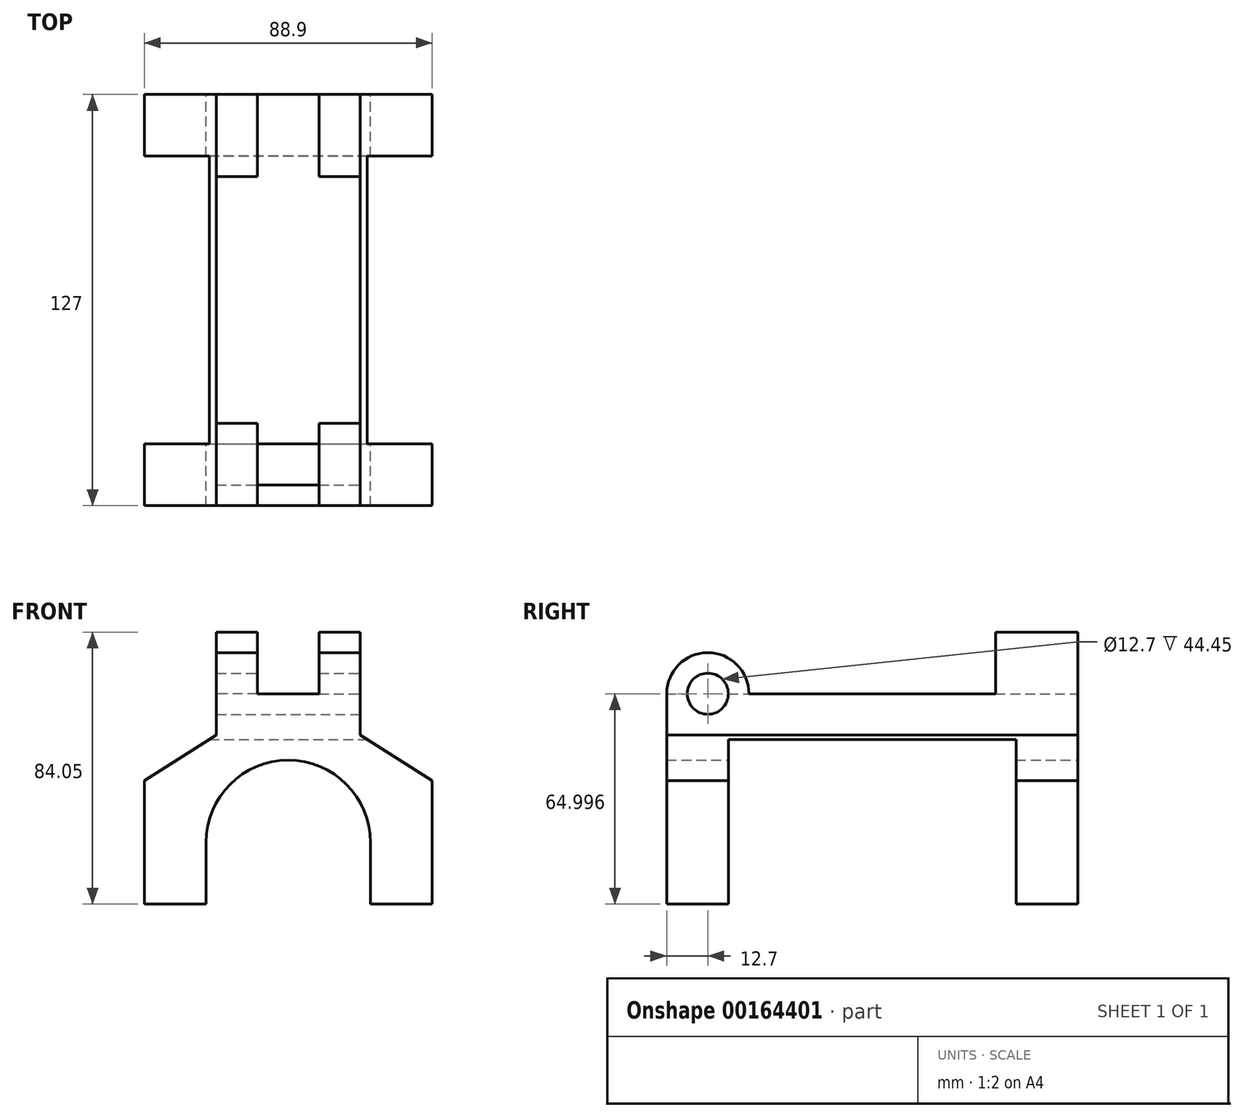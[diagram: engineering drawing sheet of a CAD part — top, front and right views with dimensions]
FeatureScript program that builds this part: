
annotation { "Feature Type Name" : "Feature", "Feature Type Description" : "" }
export const myFeature = defineFeature(function(context is Context, id is Id, definition is map)
    precondition{}
    {
        {
            var Q0;
            Q0=qCreatedBy(makeId("Front.planeOp"),FACE);
            var sketch = newSketch(context, id + "F0", { "sketchPlane" : qUnion([Q0])});
            skLineSegment(sketch, "E0.bottom", {"start": v(44.45, 0) * mm, "end": v(25.4, 0) * mm});
            skLineSegment(sketch, "E0.top", {"start": v(44.45, -19.05) * mm, "end": v(25.4, -19.05) * mm});
            skLineSegment(sketch, "E0.left", {"start": v(44.45, 0) * mm, "end": v(44.45, -19.05) * mm});
            skLineSegment(sketch, "E0.right", {"start": v(25.4, 0) * mm, "end": v(25.4, -19.05) * mm});
            skPoint(sketch, "E0.middle", {"position": v(34.92, -9.53) * mm});
            skLineSegment(sketch, "E1.bottom", {"start": v(-25.4, 0) * mm, "end": v(-44.45, 0) * mm});
            skLineSegment(sketch, "E1.top", {"start": v(-25.4, -19.05) * mm, "end": v(-44.45, -19.05) * mm});
            skLineSegment(sketch, "E1.left", {"start": v(-25.4, 0) * mm, "end": v(-25.4, -19.05) * mm});
            skLineSegment(sketch, "E1.right", {"start": v(-44.45, 0) * mm, "end": v(-44.45, -19.05) * mm});
            skPoint(sketch, "E1.middle", {"position": v(-34.93, -9.52) * mm});
            skPoint(sketch, "E1.middle.positionSnap0", {"position": v(25.4, -9.53) * mm});
            skPoint(sketch, "E1.centerSnap0", {"position": v(25.4, -9.53) * mm});
            skArc(sketch, "E2", {"start": v(25.4, 0) * mm, "mid": v(0, 25.4) * mm, "end": v(-25.4, 0) * mm});
            skLineSegment(sketch, "E3", {"start": v(44.45, 0) * mm, "end": v(44.45, 19.05) * mm});
            skLineSegment(sketch, "E4", {"start": v(-44.45, 0) * mm, "end": v(-44.45, 19.05) * mm});
            skLineSegment(sketch, "E5", {"start": v(-44.45, 19.05) * mm, "end": v(-22.23, 33.25) * mm});
            skLineSegment(sketch, "E6", {"start": v(-44.45, 19.05) * mm, "end": v(-22.23, 19.05) * mm});
            skLineSegment(sketch, "E7", {"start": v(-22.23, 19.05) * mm, "end": v(-22.23, 33.25) * mm});
            skLineSegment(sketch, "E8", {"start": v(44.45, 19.05) * mm, "end": v(22.22, 19.05) * mm});
            skLineSegment(sketch, "E9", {"start": v(22.22, 19.05) * mm, "end": v(22.22, 33.25) * mm});
            skLineSegment(sketch, "E10", {"start": v(22.22, 33.25) * mm, "end": v(44.45, 19.05) * mm});
            skLineSegment(sketch, "E11", {"start": v(22.22, 33.25) * mm, "end": v(-22.23, 33.25) * mm});
            skSolve(sketch);
        }
        {
            var Q0;
            Q0=makeQuery(id+"F0.imprint","IMPRINT",FACE,{"disambiguationData":[TD([[makeQuery(id+"F0.imprint","IMPRINT",EDGE,{"derivedFrom":sQuery(id+"F0.wireOp",EDGE,"E0.bottom")}),-1.0]])]});
            var Q1;
            Q1=makeQuery(id+"F0.imprint","IMPRINT",FACE,{"disambiguationData":[TD([[makeQuery(id+"F0.imprint","IMPRINT",EDGE,{"derivedFrom":sQuery(id+"F0.wireOp",EDGE,"E8")}),-1.0]])]});
            var Q2;
            Q2=makeQuery(id+"F0.imprint","IMPRINT",FACE,{"disambiguationData":[TD([[makeQuery(id+"F0.imprint","IMPRINT",EDGE,{"derivedFrom":sQuery(id+"F0.wireOp",EDGE,"E0.bottom")}),1.0]])]});
            var Q3;
            Q3=makeQuery(id+"F0.imprint","IMPRINT",FACE,{"disambiguationData":[TD([[makeQuery(id+"F0.imprint","IMPRINT",EDGE,{"derivedFrom":sQuery(id+"F0.wireOp",EDGE,"E1.bottom")}),1.0]])]});
            var Q4;
            Q4=makeQuery(id+"F0.imprint","IMPRINT",FACE,{"disambiguationData":[TD([[makeQuery(id+"F0.imprint","IMPRINT",EDGE,{"derivedFrom":sQuery(id+"F0.wireOp",EDGE,"E5")}),-1.0]])]});
            extrude(context, id + "F1", {"entities" : qUnion([Q0, Q1, Q2, Q3, Q4]), "depth" : 127 * mm});
        }
        {
            var Q0;
            Q0=makeQuery(id+"F1.opExtrude","SWEPT_FACE",FACE,{"disambiguationData":[OSD([sQuery(id+"F0.wireOp",EDGE,"E0.left"),sQuery(id+"F0.wireOp",EDGE,"E3")])]});
            var sketch = newSketch(context, id + "F2", { "sketchPlane" : qUnion([Q0])});
            skLineSegment(sketch, "E12", {"start": v(-127, 19.05) * mm, "end": v(-127, -19.05) * mm});
            skLineSegment(sketch, "E13", {"start": v(-107.95, -19.05) * mm, "end": v(-19.05, -19.05) * mm});
            skLineSegment(sketch, "E14", {"start": v(-107.95, -19.05) * mm, "end": v(-107.95, 19.05) * mm});
            skLineSegment(sketch, "E15", {"start": v(-19.05, -19.05) * mm, "end": v(-19.05, 19.05) * mm});
            skLineSegment(sketch, "E16", {"start": v(-107.95, 19.05) * mm, "end": v(-107.95, 31.86) * mm});
            skLineSegment(sketch, "E17", {"start": v(-107.95, 31.86) * mm, "end": v(-19.05, 31.86) * mm});
            skLineSegment(sketch, "E18", {"start": v(-19.05, 31.86) * mm, "end": v(-19.05, 19.05) * mm});
            skSolve(sketch);
        }
        {
            var Q0;
            {var subQ0=sQuery(id+"F2.wireOp",EDGE,"E16");Q0=makeQuery(id+"F2.imprint","IMPRINT",FACE,{"disambiguationData":[TD([[makeQuery(id+"F2.imprint","IMPRINT",EDGE,{"derivedFrom":subQ0}),-1.0]])]});}
            var Q1;
            Q1=makeQuery(id+"F2.imprint","IMPRINT",FACE,{"disambiguationData":[TD([[makeQuery(id+"F2.imprint","IMPRINT",EDGE,{"derivedFrom":sQuery(id+"F2.wireOp",EDGE,"E13")}),1.0]])]});
            extrude(context, id + "F3", {"entities" : qUnion([Q0, Q1]), "operationType" : NewBodyOperationType.REMOVE, "oppositeDirection" : true, "depth" : 112.01 * mm});
        }
        {
            var Q0;
            Q0=makeQuery(id+"F0.imprint","IMPRINT",FACE,{"disambiguationData":[TD([[makeQuery(id+"F0.imprint","IMPRINT",EDGE,{"derivedFrom":sQuery(id+"F0.wireOp",EDGE,"E0.bottom")}),-1.0]])]});
            var sketch = newSketch(context, id + "F4", { "sketchPlane" : qUnion([Q0])});
            skLineSegment(sketch, "E19.bottom", {"start": v(-22.23, 33.25) * mm, "end": v(22.22, 33.25) * mm});
            skLineSegment(sketch, "E19.top", {"start": v(-22.23, 45.95) * mm, "end": v(22.23, 45.95) * mm});
            skLineSegment(sketch, "E19.left", {"start": v(-22.23, 33.25) * mm, "end": v(-22.23, 45.95) * mm});
            skLineSegment(sketch, "E19.right", {"start": v(22.23, 33.25) * mm, "end": v(22.23, 45.95) * mm});
            skPoint(sketch, "E19.middle", {"position": v(0, 39.6) * mm});
            skLineSegment(sketch, "E20", {"start": v(9.52, 33.25) * mm, "end": v(9.52, 45.95) * mm});
            skLineSegment(sketch, "E21", {"start": v(9.52, 45.95) * mm, "end": v(-9.53, 45.95) * mm});
            skLineSegment(sketch, "E22", {"start": v(-9.53, 45.95) * mm, "end": v(-9.53, 33.25) * mm});
            skLineSegment(sketch, "E23", {"start": v(-9.53, 33.25) * mm, "end": v(9.52, 33.25) * mm});
            skSolve(sketch);
        }
        {
            var Q0;
            Q0=makeQuery(id+"F4.imprint","IMPRINT",FACE,{"disambiguationData":[TD([[makeQuery(id+"F4.imprint","IMPRINT",EDGE,{"derivedFrom":sQuery(id+"F4.wireOp",EDGE,"E19.bottom")}),-1.0]])]});
            extrude(context, id + "F5", {"entities" : qUnion([Q0]), "operationType" : NewBodyOperationType.ADD, "depth" : 127 * mm});
        }
        {
            var Q0;
            Q0=makeQuery(id+"F5.opExtrude","SWEPT_FACE",FACE,{"disambiguationData":[OSD([sQuery(id+"F4.wireOp",EDGE,"E19.right")])]});
            var sketch = newSketch(context, id + "F6", { "sketchPlane" : qUnion([Q0])});
            skArc(sketch, "E24", {"start": v(-101.6, 45.95) * mm, "mid": v(-114.3, 58.65) * mm, "end": v(-127, 45.95) * mm});
            skCircle(sketch, "E25", {"center": v(-114.3, 45.95) * mm, "radius": 6.35 * mm});
            skSolve(sketch);
        }
        {
            var Q0;
            {var subQ0=sQuery(id+"F6.wireOp",EDGE,"E24");Q0=makeQuery(id+"F6.imprint","IMPRINT",FACE,{"disambiguationData":[TD([[makeQuery(id+"F6.imprint","IMPRINT",EDGE,{"derivedFrom":subQ0}),1.0]])]});}
            extrude(context, id + "F7", {"entities" : qUnion([Q0]), "operationType" : NewBodyOperationType.ADD, "oppositeDirection" : true, "depth" : 12.7 * mm});
        }
        {
            var Q0;
            {var subQ0=sQuery(id+"F6.wireOp",EDGE,"E25");var subQ1=makeQuery(id+"F5.opExtrude","SWEPT_EDGE",EDGE,{"disambiguationData":[OSD([sQuery(id+"F4.wireOp",EDGE,"E19.top"),sQuery(id+"F4.wireOp",EDGE,"E19.right")])]});var subQ2=makeQuery(id+"F6.imprint","INTERSECT",VERTEX,{"disambiguationData":[OD(0.0)],"derivedFrom":[subQ1,subQ0]});Q0=makeQuery(id+"F6.imprint","IMPRINT",FACE,{"disambiguationData":[TD([[makeQuery(id+"F6.imprint","IMPRINT",EDGE,{"disambiguationData":[TD([[subQ2,-1.0]])],"derivedFrom":subQ0}),1.0]])]});}
            extrude(context, id + "F8", {"entities" : qUnion([Q0]), "operationType" : NewBodyOperationType.REMOVE, "oppositeDirection" : true, "depth" : 25.4 * mm});
        }
        {
            var Q0;
            Q0=makeQuery(id+"F5.opExtrude","SWEPT_FACE",FACE,{"disambiguationData":[OSD([sQuery(id+"F4.wireOp",EDGE,"E19.left")])]});
            var sketch = newSketch(context, id + "F9", { "sketchPlane" : qUnion([Q0])});
            skArc(sketch, "E26", {"start": v(127, 45.95) * mm, "mid": v(114.3, 58.65) * mm, "end": v(101.6, 45.95) * mm});
            skCircle(sketch, "E27", {"center": v(114.3, 45.95) * mm, "radius": 6.35 * mm});
            skSolve(sketch);
        }
        {
            var Q0;
            {var subQ0=sQuery(id+"F9.wireOp",EDGE,"E26");Q0=makeQuery(id+"F9.imprint","IMPRINT",FACE,{"disambiguationData":[TD([[makeQuery(id+"F9.imprint","IMPRINT",EDGE,{"derivedFrom":subQ0}),1.0]])]});}
            extrude(context, id + "F10", {"entities" : qUnion([Q0]), "operationType" : NewBodyOperationType.ADD, "oppositeDirection" : true, "depth" : 12.7 * mm});
        }
        {
            var Q0;
            {var subQ0=sQuery(id+"F9.wireOp",EDGE,"E27");var subQ1=makeQuery(id+"F5.opExtrude","SWEPT_EDGE",EDGE,{"disambiguationData":[OSD([sQuery(id+"F4.wireOp",EDGE,"E19.top"),sQuery(id+"F4.wireOp",EDGE,"E19.left")])]});var subQ2=makeQuery(id+"F9.imprint","INTERSECT",VERTEX,{"disambiguationData":[OD(0.0)],"derivedFrom":[subQ1,subQ0]});Q0=makeQuery(id+"F9.imprint","IMPRINT",FACE,{"disambiguationData":[TD([[makeQuery(id+"F9.imprint","IMPRINT",EDGE,{"disambiguationData":[TD([[subQ2,1.0]])],"derivedFrom":subQ0}),1.0]])]});}
            extrude(context, id + "F11", {"entities" : qUnion([Q0]), "operationType" : NewBodyOperationType.REMOVE, "oppositeDirection" : true, "depth" : 25.4 * mm});
        }
        {
            var Q0;
            {var subQ0=sQuery(id+"F4.wireOp",EDGE,"E19.left");var subQ3=makeQuery(id+"F5.opExtrude","CAP_EDGE",EDGE,{"disambiguationData":[OSD([subQ0])],"isStart":true});Q0=makeQuery(id+"F9.imprint","IMPRINT",FACE,{"disambiguationData":[TD([[makeQuery(id+"F9.imprint","IMPRINT",EDGE,{"derivedFrom":subQ3}),-1.0]])]});}
            var sketch = newSketch(context, id + "F12", { "sketchPlane" : qUnion([Q0])});
            skLineSegment(sketch, "E28", {"start": v(0, 45.95) * mm, "end": v(25.4, 45.95) * mm});
            skLineSegment(sketch, "E29", {"start": v(0, 45.95) * mm, "end": v(0, 65) * mm});
            skLineSegment(sketch, "E30", {"start": v(0, 65) * mm, "end": v(25.4, 65) * mm});
            skLineSegment(sketch, "E31", {"start": v(25.4, 45.95) * mm, "end": v(25.4, 65) * mm});
            skSolve(sketch);
        }
        {
            var Q0;
            Q0=makeQuery(id+"F12.imprint","IMPRINT",FACE,{"disambiguationData":[TD([[makeQuery(id+"F12.imprint","IMPRINT",EDGE,{"derivedFrom":sQuery(id+"F12.wireOp",EDGE,"E28")}),-1.0]])]});
            extrude(context, id + "F13", {"entities" : qUnion([Q0]), "operationType" : NewBodyOperationType.ADD, "oppositeDirection" : true, "depth" : 12.7 * mm});
        }
        {
            var Q0;
            {var subQ0=sQuery(id+"F4.wireOp",EDGE,"E19.right");var subQ3=makeQuery(id+"F5.opExtrude","CAP_EDGE",EDGE,{"disambiguationData":[OSD([subQ0])],"isStart":true});Q0=makeQuery(id+"F6.imprint","IMPRINT",FACE,{"disambiguationData":[TD([[makeQuery(id+"F6.imprint","IMPRINT",EDGE,{"derivedFrom":subQ3}),1.0]])]});}
            var sketch = newSketch(context, id + "F14", { "sketchPlane" : qUnion([Q0])});
            skLineSegment(sketch, "E32.bottom", {"start": v(8.6, 45.95) * mm, "end": v(8.6, 45.95) * mm});
            skLineSegment(sketch, "E32.left", {"start": v(8.6, 45.95) * mm, "end": v(8.6, 45.93) * mm});
            skLineSegment(sketch, "E32.right", {"start": v(8.6, 45.95) * mm, "end": v(8.6, 45.93) * mm});
            skLineSegment(sketch, "E33", {"start": v(0, 45.95) * mm, "end": v(-25.4, 45.95) * mm});
            skLineSegment(sketch, "E34", {"start": v(0, 45.95) * mm, "end": v(0, 65) * mm});
            skLineSegment(sketch, "E35", {"start": v(0, 65) * mm, "end": v(-25.4, 65) * mm});
            skLineSegment(sketch, "E36", {"start": v(-25.4, 65) * mm, "end": v(-25.4, 45.95) * mm});
            skSolve(sketch);
        }
        {
            var Q0;
            Q0=makeQuery(id+"F14.imprint","IMPRINT",FACE,{"disambiguationData":[TD([[makeQuery(id+"F14.imprint","IMPRINT",EDGE,{"derivedFrom":sQuery(id+"F14.wireOp",EDGE,"E33")}),1.0]])]});
            extrude(context, id + "F15", {"entities" : qUnion([Q0]), "operationType" : NewBodyOperationType.ADD, "oppositeDirection" : true, "depth" : 12.7 * mm});
        }
    });
